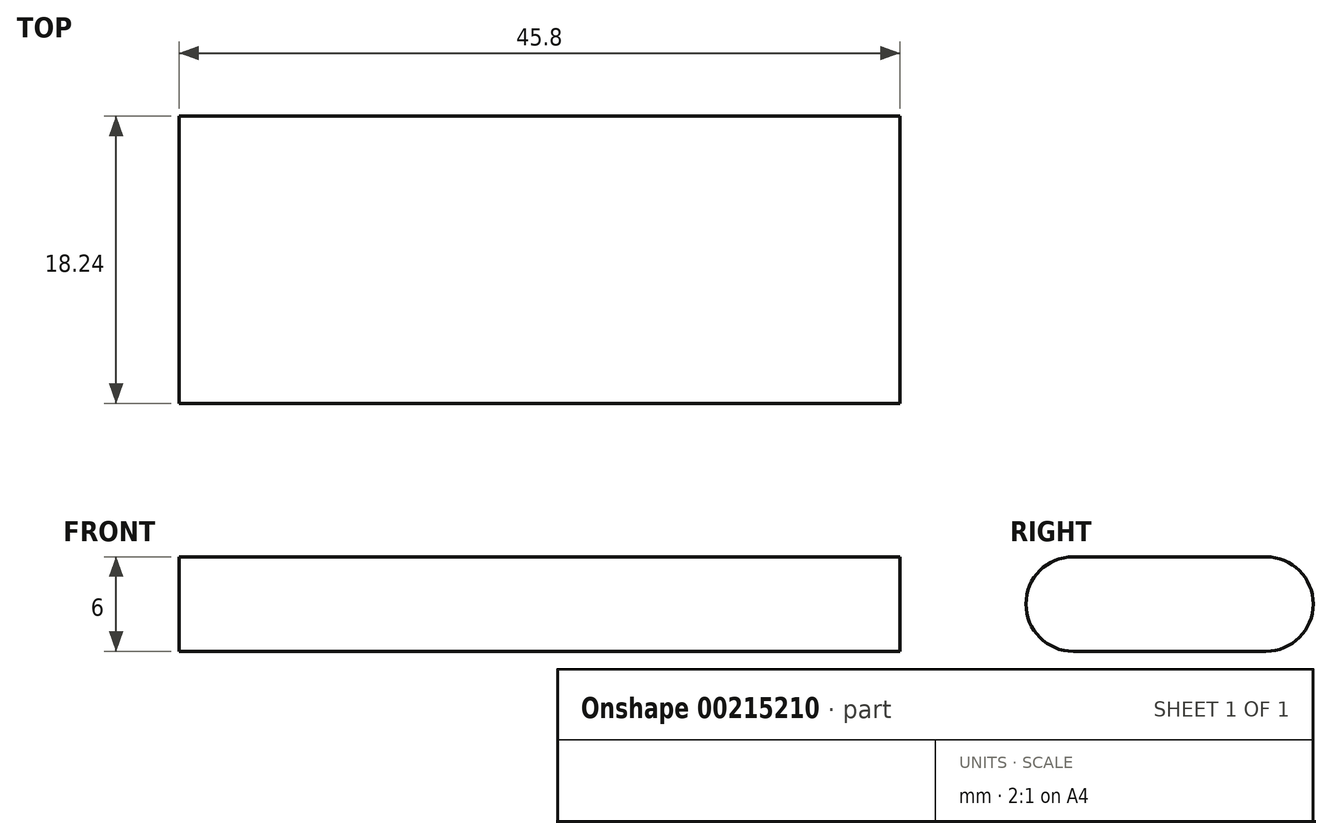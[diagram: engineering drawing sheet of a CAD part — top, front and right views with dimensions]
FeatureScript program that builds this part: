
annotation { "Feature Type Name" : "Feature", "Feature Type Description" : "" }
export const myFeature = defineFeature(function(context is Context, id is Id, definition is map)
    precondition{}
    {
        {
            var Q0;
            Q0=qCreatedBy(makeId("Top.planeOp"),FACE);
            var sketch = newSketch(context, id + "F0", { "sketchPlane" : qUnion([Q0])});
            skLineSegment(sketch, "E0.bottom", {"start": v(22.9, 9.13) * mm, "end": v(-22.9, 9.13) * mm});
            skLineSegment(sketch, "E0.top", {"start": v(22.9, -9.12) * mm, "end": v(-22.9, -9.12) * mm});
            skLineSegment(sketch, "E0.left", {"start": v(22.9, 9.13) * mm, "end": v(22.9, -9.12) * mm});
            skLineSegment(sketch, "E0.right", {"start": v(-22.9, 9.13) * mm, "end": v(-22.9, -9.12) * mm});
            skPoint(sketch, "E0.middle", {"position": v(0, 0) * mm});
            skSolve(sketch);
        }
        {
            var Q0;
            Q0=makeQuery(id+"F0.imprint","IMPRINT",FACE,{"disambiguationData":[TD([[makeQuery(id+"F0.imprint","IMPRINT",EDGE,{"derivedFrom":sQuery(id+"F0.wireOp",EDGE,"E0.bottom")}),1.0]])]});
            extrude(context, id + "F1", {"entities" : qUnion([Q0]), "depth" : 6 * mm});
        }
        {
            var Q0;
            Q0=makeQuery(id+"F1.opExtrude","CAP_EDGE",EDGE,{"disambiguationData":[OSD([sQuery(id+"F0.wireOp",EDGE,"E0.top")])],"isStart":false});
            var Q1;
            Q1=makeQuery(id+"F1.opExtrude","CAP_EDGE",EDGE,{"disambiguationData":[OSD([sQuery(id+"F0.wireOp",EDGE,"E0.top")])],"isStart":true});
            var Q2;
            Q2=makeQuery(id+"F1.opExtrude","CAP_EDGE",EDGE,{"disambiguationData":[OSD([sQuery(id+"F0.wireOp",EDGE,"E0.bottom")])],"isStart":false});
            var Q3;
            Q3=makeQuery(id+"F1.opExtrude","CAP_EDGE",EDGE,{"disambiguationData":[OSD([sQuery(id+"F0.wireOp",EDGE,"E0.bottom")])],"isStart":true});
            fillet(context, id + "F2", {"entities" : qUnion([Q0, Q1, Q2, Q3]), "radius" : 3 * mm, "tangentPropagation" : true, "allowEdgeOverflow" : false});
        }
    });
